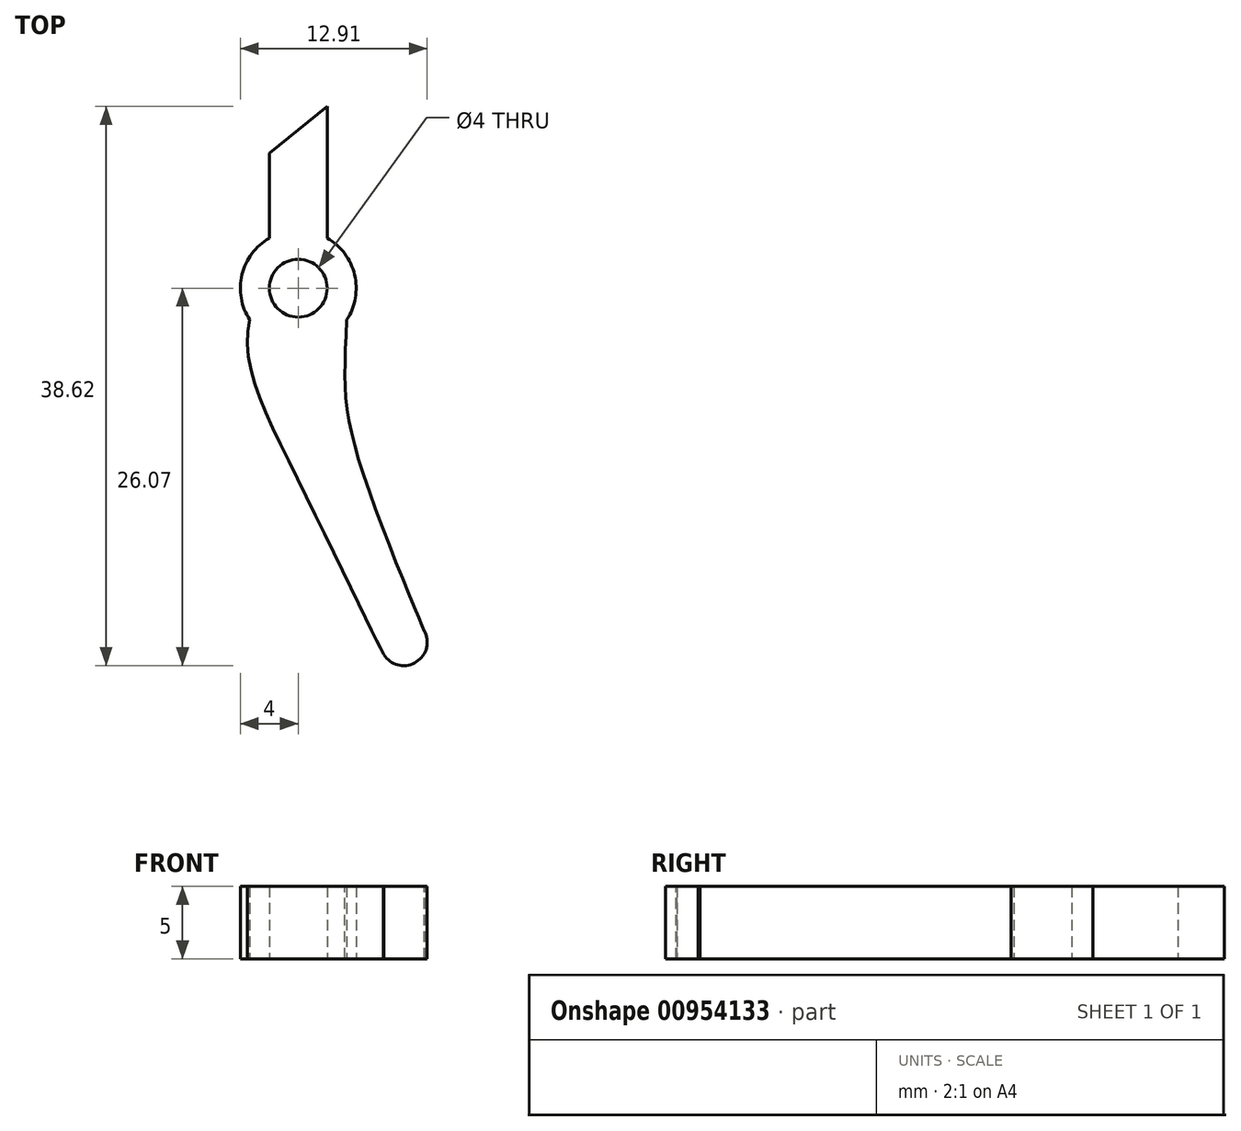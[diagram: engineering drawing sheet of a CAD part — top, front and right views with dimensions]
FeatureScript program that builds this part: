
annotation { "Feature Type Name" : "Feature", "Feature Type Description" : "" }
export const myFeature = defineFeature(function(context is Context, id is Id, definition is map)
    precondition{}
    {
        {
            var Q0;
            Q0=qCreatedBy(makeId("Top.planeOp"),FACE);
            var sketch = newSketch(context, id + "F0", { "sketchPlane" : qUnion([Q0])});
            skCircle(sketch, "E0", {"center": v(0, 0) * mm, "radius": 2 * mm});
            skCircle(sketch, "E1.0", {"center": v(0, 0) * mm, "radius": 4 * mm});
            skLineSegment(sketch, "E2", {"start": v(-2, 3.46) * mm, "end": v(-2, 9.33) * mm});
            skLineSegment(sketch, "E3", {"start": v(2, 3.46) * mm, "end": v(2, 12.55) * mm});
            skLineSegment(sketch, "E4", {"start": v(2, 12.55) * mm, "end": v(-2, 9.33) * mm});
            skCircle(sketch, "E5", {"center": v(7.29, -24.45) * mm, "radius": 1.62 * mm});
            skPoint(sketch, "E5.second.point", {"position": v(7.03, -26.05) * mm});
            skPoint(sketch, "E5.third.point", {"position": v(7.76, -26) * mm});
            skFitSpline(sketch, "E6", {"points": [v(-3.35, -2.18) * mm, v(0, -13.27) * mm, v(5.85, -25.2) * mm, v(5.91, -25.32) * mm, v(5.89, -25.27) * mm], "startDerivative": vector(-5.24, -19.9) * mm, "endDerivative": vector(-1.33, 1.88) * mm});
            skFitSpline(sketch, "E7", {"points": [v(3.35, -2.18) * mm, v(4.28, -12.16) * mm, v(8.77, -23.8) * mm, v(8.77, -23.78) * mm], "startDerivative": vector(-1.36, -27.8) * mm, "endDerivative": vector(-0.93, 1.16) * mm});
            skSolve(sketch);
        }
        {
            var Q0;
            Q0=makeQuery(id+"F0.imprint","IMPRINT",FACE,{"disambiguationData":[TD([[makeQuery(id+"F0.imprint","IMPRINT",EDGE,{"derivedFrom":sQuery(id+"F0.wireOp",EDGE,"E0")}),-1.0]])]});
            var Q1;
            {var subQ0=sQuery(id+"F0.wireOp",EDGE,"E2");Q1=makeQuery(id+"F0.imprint","IMPRINT",FACE,{"disambiguationData":[TD([[makeQuery(id+"F0.imprint","IMPRINT",EDGE,{"derivedFrom":subQ0}),-1.0]])]});}
            var Q2;
            {var subQ0=sQuery(id+"F0.wireOp",EDGE,"fc5fd2b8-8430-4a82-a448-7aca27a5b1a2");var subQ1=sQuery(id+"F0.wireOp",EDGE,"E1.0");var subQ2=makeQuery(id+"F0.imprint","INTERSECT",VERTEX,{"derivedFrom":[subQ1,subQ0]});Q2=makeQuery(id+"F0.imprint","IMPRINT",FACE,{"disambiguationData":[TD([[makeQuery(id+"F0.imprint","IMPRINT",EDGE,{"disambiguationData":[TD([[subQ2,1.0]])],"derivedFrom":subQ1}),-1.0]])]});}
            var Q3;
            {var subQ0=sQuery(id+"F0.wireOp",EDGE,"E5");var subQ1=sQuery(id+"F0.wireOp",EDGE,"fc5fd2b8-8430-4a82-a448-7aca27a5b1a2");var subQ2=makeQuery(id+"F0.imprint","INTERSECT",VERTEX,{"disambiguationData":[OD(0.0)],"derivedFrom":[subQ1,subQ0]});Q3=makeQuery(id+"F0.imprint","IMPRINT",FACE,{"disambiguationData":[TD([[makeQuery(id+"F0.imprint","IMPRINT",EDGE,{"disambiguationData":[TD([[subQ2,1.0]])],"derivedFrom":subQ1}),-1.0]])]});}
            var Q4;
            {var subQ0=sQuery(id+"F0.wireOp",EDGE,"E7");var subQ1=sQuery(id+"F0.wireOp",EDGE,"E5");var subQ2=makeQuery(id+"F0.imprint","INTERSECT",VERTEX,{"disambiguationData":[OD(2.0)],"derivedFrom":[subQ1,subQ0]});Q4=makeQuery(id+"F0.imprint","IMPRINT",FACE,{"disambiguationData":[TD([[makeQuery(id+"F0.imprint","IMPRINT",EDGE,{"disambiguationData":[TD([[subQ2,-1.0]])],"derivedFrom":subQ1}),1.0]])]});}
            extrude(context, id + "F1", {"entities" : qUnion([Q0, Q1, Q2, Q3, Q4]), "depth" : 5 * mm, "offsetDistance" : 25 * mm});
        }
    });
